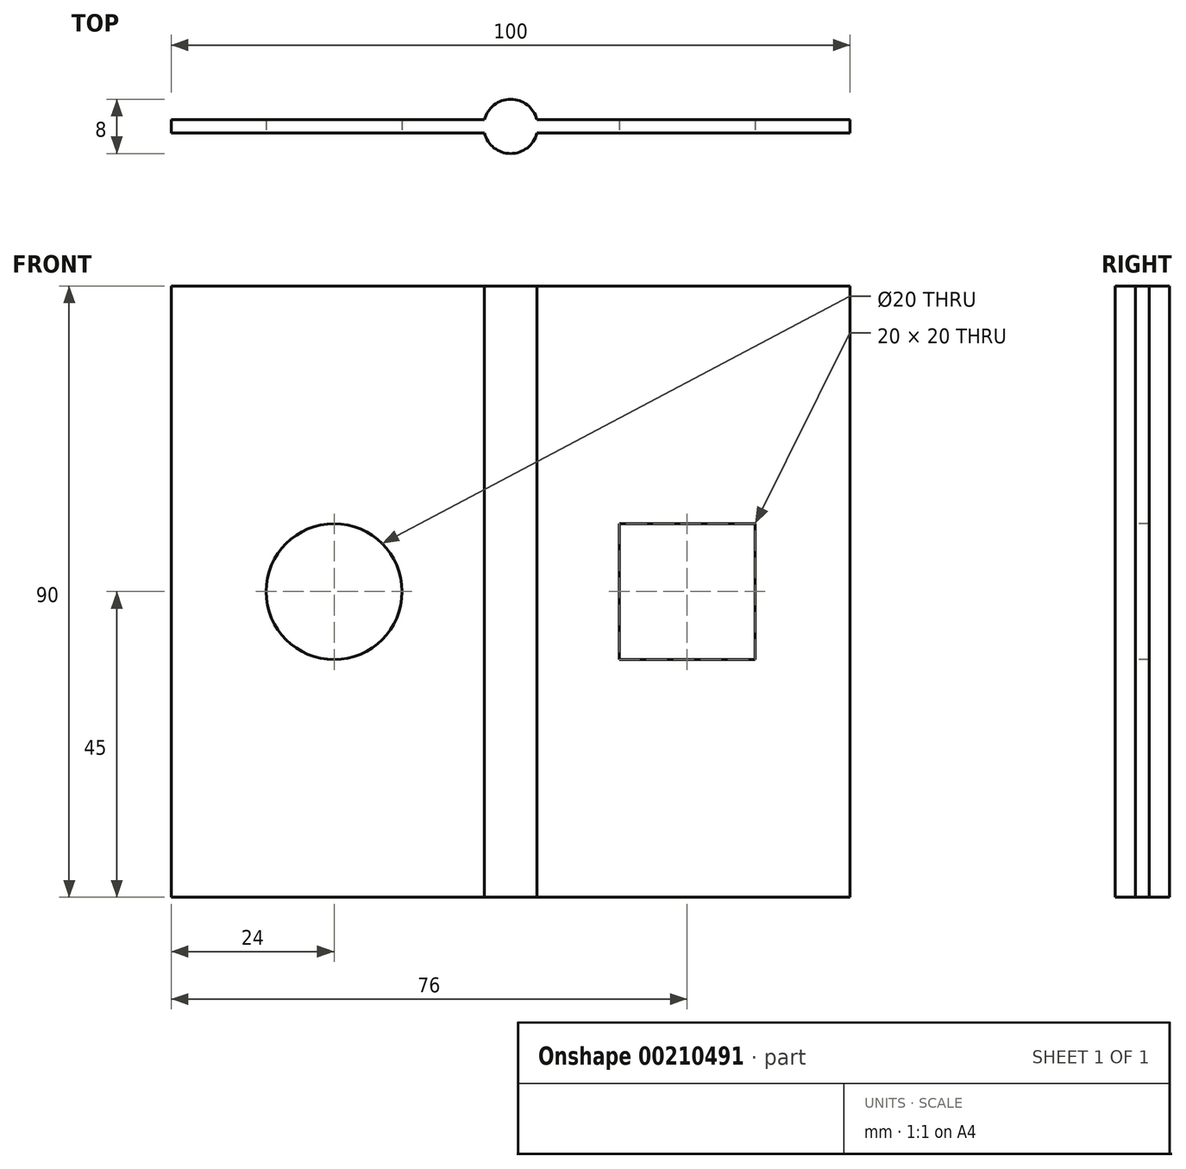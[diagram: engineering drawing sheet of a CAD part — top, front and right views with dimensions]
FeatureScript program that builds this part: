
annotation { "Feature Type Name" : "Feature", "Feature Type Description" : "" }
export const myFeature = defineFeature(function(context is Context, id is Id, definition is map)
    precondition{}
    {
        {
            var Q0;
            Q0=qCreatedBy(makeId("Top.planeOp"),FACE);
            var sketch = newSketch(context, id + "F0", { "sketchPlane" : qUnion([Q0])});
            skCircle(sketch, "E0", {"center": v(0, 0) * mm, "radius": 4 * mm});
            skLineSegment(sketch, "E1", {"start": v(-50, -1) * mm, "end": v(-3.87, -1) * mm});
            skLineSegment(sketch, "E2", {"start": v(-50, 1) * mm, "end": v(-50, -1) * mm});
            skLineSegment(sketch, "E3", {"start": v(-50, 1) * mm, "end": v(-3.87, 1) * mm});
            skCircle(sketch, "E4", {"center": v(0, 0) * mm, "radius": 2 * mm});
            skLineSegment(sketch, "E5.MirrorCS", {"start": v(50, 1) * mm, "end": v(3.87, 1) * mm});
            skLineSegment(sketch, "E6.MirrorCS", {"start": v(50, -1) * mm, "end": v(3.87, -1) * mm});
            skLineSegment(sketch, "E7.MirrorCS", {"start": v(50, 1) * mm, "end": v(50, -1) * mm});
            skSolve(sketch);
        }
        {
            var Q0;
            Q0=makeQuery(id+"F0.imprint","IMPRINT",FACE,{"disambiguationData":[TD([[makeQuery(id+"F0.imprint","IMPRINT",EDGE,{"derivedFrom":sQuery(id+"F0.wireOp",EDGE,"E4")}),1.0]])]});
            extrude(context, id + "F1", {"entities" : qUnion([Q0]), "depth" : 90 * mm, "symmetric" : true});
        }
        {
            var Q0;
            {var subQ0=sQuery(id+"F0.wireOp",EDGE,"E1");Q0=makeQuery(id+"F0.imprint","IMPRINT",FACE,{"disambiguationData":[TD([[makeQuery(id+"F0.imprint","IMPRINT",EDGE,{"derivedFrom":subQ0}),1.0]])]});}
            extrude(context, id + "F2", {"entities" : qUnion([Q0]), "depth" : 90 * mm, "symmetric" : true});
        }
        {
            var Q0;
            Q0=makeQuery(id+"F0.imprint","IMPRINT",FACE,{"disambiguationData":[TD([[makeQuery(id+"F0.imprint","IMPRINT",EDGE,{"derivedFrom":sQuery(id+"F0.wireOp",EDGE,"E4")}),-1.0]])]});
            extrude(context, id + "F3", {"entities" : qUnion([Q0]), "operationType" : NewBodyOperationType.ADD, "depth" : 30 * mm, "symmetric" : true});
        }
        {
            var Q0;
            {var subQ0=sQuery(id+"F0.wireOp",EDGE,"E5.MirrorCS");Q0=makeQuery(id+"F0.imprint","IMPRINT",FACE,{"disambiguationData":[TD([[makeQuery(id+"F0.imprint","IMPRINT",EDGE,{"derivedFrom":subQ0}),1.0]])]});}
            extrude(context, id + "F4", {"entities" : qUnion([Q0]), "depth" : 90 * mm, "symmetric" : true});
        }
        {
            var Q0;
            Q0=makeQuery(id+"F3.opExtrude","CAP_FACE",FACE,{"disambiguationData":[OSD([sQuery(id+"F0.wireOp",EDGE,"E0"),sQuery(id+"F0.wireOp",EDGE,"E4")])],"isStart":false});
            var Q1;
            Q1=makeQuery(id+"F4.opExtrude","CAP_FACE",FACE,{"disambiguationData":[OSD([sQuery(id+"F0.wireOp",EDGE,"E0"),sQuery(id+"F0.wireOp",EDGE,"E5.MirrorCS"),sQuery(id+"F0.wireOp",EDGE,"E6.MirrorCS"),sQuery(id+"F0.wireOp",EDGE,"E7.MirrorCS")])],"isStart":false});
            extrude(context, id + "F5", {"entities" : qUnion([Q0]), "operationType" : NewBodyOperationType.ADD, "endBound" : BoundingType.UP_TO_SURFACE, "endBoundEntityFace" : qUnion([Q1]), "depth" : 25 * mm});
        }
        {
            var Q0;
            Q0=makeQuery(id+"F3.opExtrude","CAP_FACE",FACE,{"disambiguationData":[OSD([sQuery(id+"F0.wireOp",EDGE,"E0"),sQuery(id+"F0.wireOp",EDGE,"E4")])],"isStart":true});
            var Q1;
            Q1=makeQuery(id+"F4.opExtrude","CAP_FACE",FACE,{"disambiguationData":[OSD([sQuery(id+"F0.wireOp",EDGE,"E0"),sQuery(id+"F0.wireOp",EDGE,"E5.MirrorCS"),sQuery(id+"F0.wireOp",EDGE,"E6.MirrorCS"),sQuery(id+"F0.wireOp",EDGE,"E7.MirrorCS")])],"isStart":true});
            var Q2;
            Q2=makeQuery(id+"F4.opExtrude","SWEPT_BODY",BODY,{"disambiguationData":[OSD([sQuery(id+"F0.wireOp",EDGE,"E0"),sQuery(id+"F0.wireOp",EDGE,"E5.MirrorCS"),sQuery(id+"F0.wireOp",EDGE,"E6.MirrorCS"),sQuery(id+"F0.wireOp",EDGE,"E7.MirrorCS")])]});
            extrude(context, id + "F6", {"entities" : qUnion([Q0]), "operationType" : NewBodyOperationType.ADD, "endBound" : BoundingType.UP_TO_SURFACE, "endBoundEntityFace" : qUnion([Q1]), "endBoundEntityBody" : qUnion([Q2]), "depth" : 25 * mm});
        }
        {
            var Q0;
            Q0=makeQuery(id+"F2.opExtrude","SWEPT_FACE",FACE,{"disambiguationData":[OSD([sQuery(id+"F0.wireOp",EDGE,"E1")])]});
            var sketch = newSketch(context, id + "F7", { "sketchPlane" : qUnion([Q0])});
            skCircle(sketch, "E8", {"center": v(-26, 0) * mm, "radius": 10 * mm});
            skSolve(sketch);
        }
        {
            var Q0;
            Q0=makeQuery(id+"F7.imprint","IMPRINT",FACE,{"disambiguationData":[TD([[makeQuery(id+"F7.imprint","IMPRINT",EDGE,{"derivedFrom":sQuery(id+"F7.wireOp",EDGE,"E8")}),1.0]])]});
            extrude(context, id + "F8", {"entities" : qUnion([Q0]), "operationType" : NewBodyOperationType.REMOVE, "endBound" : BoundingType.THROUGH_ALL, "oppositeDirection" : true, "depth" : 25 * mm});
        }
        {
            var Q0;
            Q0=makeQuery(id+"F4.opExtrude","SWEPT_FACE",FACE,{"disambiguationData":[OSD([sQuery(id+"F0.wireOp",EDGE,"E6.MirrorCS")])]});
            var sketch = newSketch(context, id + "F9", { "sketchPlane" : qUnion([Q0])});
            skLineSegment(sketch, "E9.bottom", {"start": v(16, 10) * mm, "end": v(36, 10) * mm});
            skLineSegment(sketch, "E9.top", {"start": v(16, -10) * mm, "end": v(36, -10) * mm});
            skLineSegment(sketch, "E9.left", {"start": v(16, 10) * mm, "end": v(16, -10) * mm});
            skLineSegment(sketch, "E9.right", {"start": v(36, 10) * mm, "end": v(36, -10) * mm});
            skPoint(sketch, "E9.middle", {"position": v(26, 0) * mm});
            skSolve(sketch);
        }
        {
            var Q0;
            Q0=makeQuery(id+"F9.imprint","IMPRINT",FACE,{"disambiguationData":[TD([[makeQuery(id+"F9.imprint","IMPRINT",EDGE,{"derivedFrom":sQuery(id+"F9.wireOp",EDGE,"E9.bottom")}),-1.0]])]});
            extrude(context, id + "F10", {"entities" : qUnion([Q0]), "operationType" : NewBodyOperationType.REMOVE, "endBound" : BoundingType.THROUGH_ALL, "oppositeDirection" : true, "depth" : 25 * mm});
        }
    });
